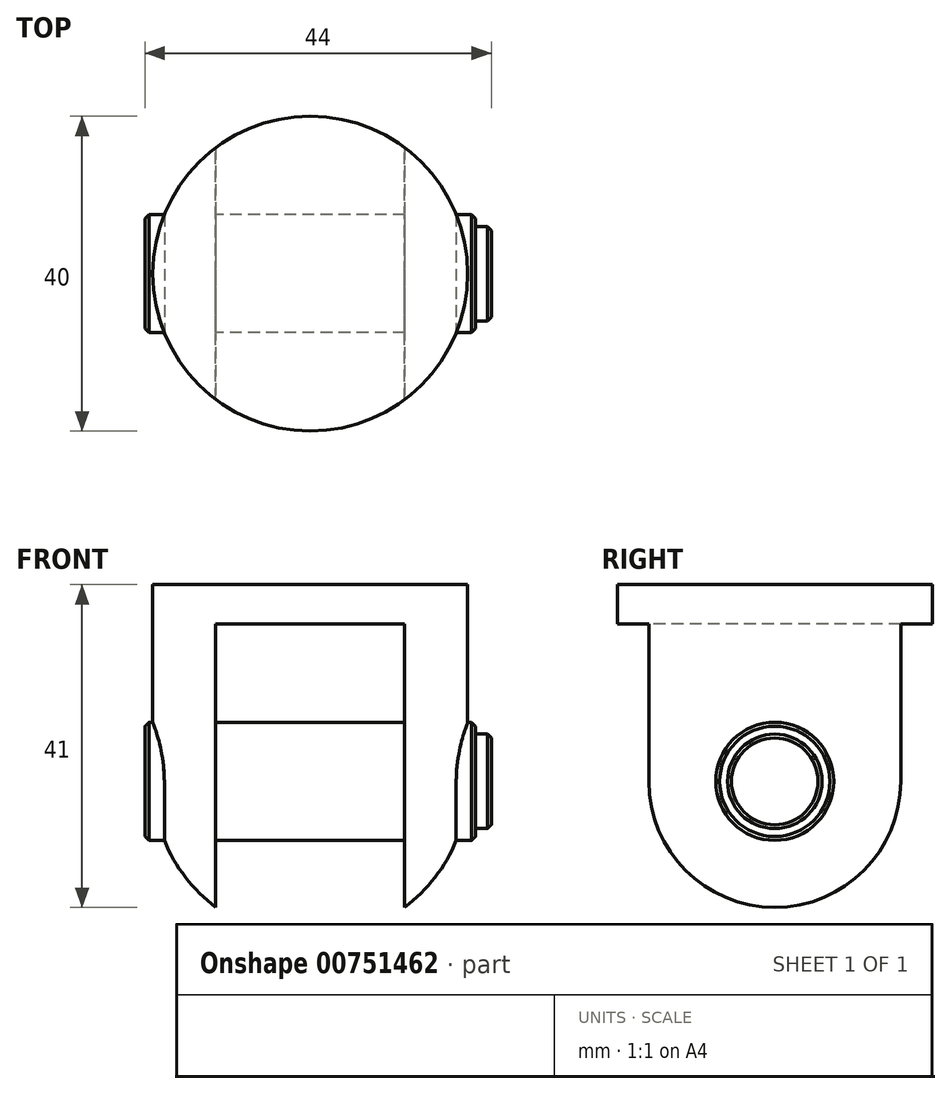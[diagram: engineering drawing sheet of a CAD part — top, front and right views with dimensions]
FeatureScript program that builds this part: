
annotation { "Feature Type Name" : "Feature", "Feature Type Description" : "" }
export const myFeature = defineFeature(function(context is Context, id is Id, definition is map)
    precondition{}
    {
        {
            var Q0;
            Q0=qCreatedBy(makeId("Front.planeOp"),FACE);
            var sketch = newSketch(context, id + "F0", { "sketchPlane" : qUnion([Q0])});
            skLineSegment(sketch, "E0", {"start": v(0, 0) * mm, "end": v(20, 0) * mm});
            skLineSegment(sketch, "E1", {"start": v(20, 0) * mm, "end": v(20, -25) * mm});
            skArc(sketch, "E2", {"start": v(0, -45) * mm, "mid": v(14.14, -39.14) * mm, "end": v(20, -25) * mm});
            skLineSegment(sketch, "E3", {"start": v(0, 0) * mm, "end": v(0, -45) * mm});
            skLineSegment(sketch, "E4", {"start": v(0, 0) * mm, "end": v(0, 8.72) * mm, "construction": true});
            skLineSegment(sketch, "E5", {"start": v(0, -25) * mm, "end": v(20, -25) * mm, "construction": true});
            skArc(sketch, "E6", {"start": v(20, -25) * mm, "mid": v(14.14, -10.86) * mm, "end": v(0, -5) * mm, "construction": true});
            skLineSegment(sketch, "E7", {"start": v(0, -5) * mm, "end": v(20, -5) * mm, "construction": true});
            skLineSegment(sketch, "E8", {"start": v(12, -5) * mm, "end": v(12, -45) * mm, "construction": true});
            skLineSegment(sketch, "E9", {"start": v(12, -45) * mm, "end": v(0, -45) * mm, "construction": true});
            skSolve(sketch);
        }
        {
            var Q0;
            Q0=qSketchRegion(id+"F0",true);
            var Q1;
            Q1=sQuery(id+"F0.wireOp",EDGE,"E4");
            revolve(context, id + "F1", {"surfaceOperationType" : NewSurfaceOperationType.NEW, "entities" : qUnion([Q0]), "axis" : qUnion([Q1]), "revolveType" : RevolveType.FULL});
        }
        {
            var Q0;
            Q0=qCreatedBy(makeId("Front.planeOp"),FACE);
            var sketch = newSketch(context, id + "F2", { "sketchPlane" : qUnion([Q0])});
            skLineSegment(sketch, "E10", {"start": v(12, -45) * mm, "end": v(12, -5) * mm});
            skLineSegment(sketch, "E11", {"start": v(12, -5) * mm, "end": v(0, -5) * mm});
            skLineSegment(sketch, "E12", {"start": v(0, -5) * mm, "end": v(0, -45) * mm, "construction": true});
            skLineSegment(sketch, "E13", {"start": v(0, -45) * mm, "end": v(12, -45) * mm});
            skLineSegment(sketch, "E14.MirrorCS", {"start": v(0, -45) * mm, "end": v(-12, -45) * mm});
            skLineSegment(sketch, "E15.MirrorCS", {"start": v(-12, -45) * mm, "end": v(-12, -5) * mm});
            skLineSegment(sketch, "E16.MirrorCS", {"start": v(-12, -5) * mm, "end": v(0, -5) * mm});
            skSolve(sketch);
        }
        {
            var Q0;
            Q0=qSketchRegion(id+"F2",true);
            extrude(context, id + "F3", {"entities" : qUnion([Q0]), "operationType" : NewBodyOperationType.REMOVE, "endBound" : BoundingType.THROUGH_ALL, "oppositeDirection" : true, "depth" : 25 * mm, "offsetDistance" : 25 * mm, "hasSecondDirection" : true, "secondDirectionBound" : SecondDirectionBoundingType.THROUGH_ALL, "secondDirectionOppositeDirection" : false, "secondDirectionDepth" : 25 * mm});
        }
        {
            var Q0;
            Q0=qCreatedBy(makeId("Right.planeOp"),FACE);
            var sketch = newSketch(context, id + "F4", { "sketchPlane" : qUnion([Q0])});
            skCircle(sketch, "E17", {"center": v(0, -25) * mm, "radius": 7.5 * mm});
            skSolve(sketch);
        }
        {
            var Q0;
            Q0=qSketchRegion(id+"F4",true);
            var Q1;
            Q1=sQuery(id+"F0.wireOp",VERTEX,"E1.end");
            extrude(context, id + "F5", {"entities" : qUnion([Q0]), "operationType" : NewBodyOperationType.ADD, "endBound" : BoundingType.UP_TO_VERTEX, "depth" : 25 * mm, "endBoundEntityVertex" : qUnion([Q1]), "hasOffset" : true, "offsetDistance" : 1 * mm, "offsetOppositeDirection" : true});
        }
        {
            var Q0;
            Q0=makeQuery(id+"F1.opRevolve","SWEPT_BODY",BODY,{"disambiguationData":[OSD([sQuery(id+"F0.wireOp",EDGE,"E0"),sQuery(id+"F0.wireOp",EDGE,"E1"),sQuery(id+"F0.wireOp",EDGE,"E2"),sQuery(id+"F0.wireOp",EDGE,"E3")])]});
            var Q1;
            Q1=qCreatedBy(makeId("Right.planeOp"),FACE);
            mirror(context, id + "F6", {"operationType" : NewBodyOperationType.ADD, "entities" : qUnion([Q0]), "mirrorPlane" : qUnion([Q1])});
        }
        {
            var Q0;
            Q0=makeQuery(id+"F5.opExtrude","CAP_FACE",FACE,{"disambiguationData":[OSD([sQuery(id+"F4.wireOp",EDGE,"E17")])],"isStart":false});
            var sketch = newSketch(context, id + "F7", { "sketchPlane" : qUnion([Q0])});
            skCircle(sketch, "E18", {"center": v(0, -25) * mm, "radius": 6 * mm});
            skSolve(sketch);
        }
        {
            var Q0;
            Q0=qSketchRegion(id+"F7",true);
            var Q1;
            Q1=makeQuery(id+"F3.boolean.opBoolean","COPY",FACE,{"derivedFrom":makeQuery(id+"F3.opExtrude","SWEPT_FACE",FACE,{"disambiguationData":[OSD([sQuery(id+"F2.wireOp",EDGE,"E10")])]})});
            var Q2;
            Q2=makeQuery(id+"F1.opRevolve","SWEPT_BODY",BODY,{"disambiguationData":[OSD([sQuery(id+"F0.wireOp",EDGE,"E0"),sQuery(id+"F0.wireOp",EDGE,"E1"),sQuery(id+"F0.wireOp",EDGE,"E2"),sQuery(id+"F0.wireOp",EDGE,"E3")])]});
            extrude(context, id + "F8", {"entities" : qUnion([Q0]), "operationType" : NewBodyOperationType.ADD, "depth" : 2 * mm, "offsetDistance" : 25 * mm, "hasSecondDirection" : true, "secondDirectionBound" : SecondDirectionBoundingType.UP_TO_SURFACE, "secondDirectionOppositeDirection" : true, "secondDirectionDepth" : 25 * mm, "secondDirectionBoundEntityFace" : qUnion([Q1]), "secondDirectionBoundEntityBody" : qUnion([Q2])});
        }
        {
            var Q0;
            Q0=makeQuery(id+"F8.opExtrude","CAP_EDGE",EDGE,{"disambiguationData":[OSD([sQuery(id+"F7.wireOp",EDGE,"E18")])],"isStart":false});
            var Q1;
            Q1=makeQuery(id+"F6.opPattern","COPY",EDGE,{"derivedFrom":makeQuery(id+"F5.opExtrude","CAP_EDGE",EDGE,{"disambiguationData":[OSD([sQuery(id+"F4.wireOp",EDGE,"E17")])],"isStart":false}),"instanceName":"1"});
            var Q2;
            Q2=makeQuery(id+"F5.opExtrude","CAP_EDGE",EDGE,{"disambiguationData":[OSD([sQuery(id+"F4.wireOp",EDGE,"E17")])],"isStart":false});
            chamfer(context, id + "F9", {"entities" : qUnion([Q0, Q1, Q2]), "width" : 0.5 * mm, "tangentPropagation" : true});
        }
    });
